# Revit family: IQ8Alarm
name_source: partatom
category: Fire Alarm Devices
revit_build: Autodesk Revit 2014 (Build: 20130308_1515(x64)
units: mm (PartAtom-declared; Revit-internal decimal feet)

## types (6) — shared parameters
Manufacturer = Esser by Honeywell
URL = https://www.esser-systems.com
b5 = 7 mm  [stored 0.0229659 ft]
content_date_modified = 16.06.2015
content_version = 1.0
h1 = 112 mm  [stored 0.367454 ft]
l1 = 112 mm  [stored 0.367454 ft]
l2 = 40 mm  [stored 0.131234 ft]
l3 = 20 mm  [stored 0.0656168 ft]
o1 = 8 mm  [stored 0.0262467 ft]
o2 = 2 mm  [stored 0.00656168 ft]
o3 = 1 mm  [stored 0.00328084 ft]
o5 = 1 mm  [stored 0.00328084 ft]
o6 = 15 mm  [stored 0.0492126 ft]
r1 = 50 mm  [stored 0.164042 ft]
type of detector = 99
zero-valued in all types: o4

## per-type parameters (varying)
| type | Model | article number | b1 | b2 | b3 | b4 | material |
| IQ8Alarm/So signaler with isolator Red | IQ8Alarm/So signaler with isolator, red | 807206 | 75 mm | 60 mm  [stored 0.19685 ft] | 25 mm  [stored 0.082021 ft] | 12 mm  [stored 0.0393701 ft] | Red |
| IQ8Alarm/So signaler with isolator White | IQ8Alarm/So signaler with isolator, white | 807205 | 75 mm | 60 mm  [stored 0.19685 ft] | 25 mm  [stored 0.082021 ft] | 12 mm  [stored 0.0393701 ft] | White |
| IQ8Alarm/Sp signaler with isolator Red | IQ8Alarm/Sp signaler with isolator, red | 807332 | 75 mm | 60 mm  [stored 0.19685 ft] | 25 mm  [stored 0.082021 ft] | 12 mm  [stored 0.0393701 ft] | Red |
| IQ8Alarm/FSo signaler with isolator Red | IQ8Alarm/FSo signaler with isolator, red | 807224 | 75 mm | 60 mm  [stored 0.19685 ft] | 25 mm  [stored 0.082021 ft] | 12 mm  [stored 0.0393701 ft] | Red |
| IQ8Alarm/FSp signaler with isolator Red | IQ8Alarm/FSp signaler with isolator, red | 807372 | 75 mm | 60 mm  [stored 0.19685 ft] | 25 mm  [stored 0.082021 ft] | 12 mm  [stored 0.0393701 ft] | Red |
| IQ8Alarm/F signaler with isolator Red flash | IQ8Alarm/F signaler with isolator, red flash | 807214 | 90 mm  [stored 0.295276 ft] | 75 mm | 60 mm  [stored 0.19685 ft] | 45 mm  [stored 0.147638 ft] | Red |

note: [stored X ft] marks values corroborated as IEEE doubles in the binary element streams (Revit-internal decimal feet)

## geometry (parser evidence)
native form markers: Sweep x3
no freeform markers — native parametric forms only
